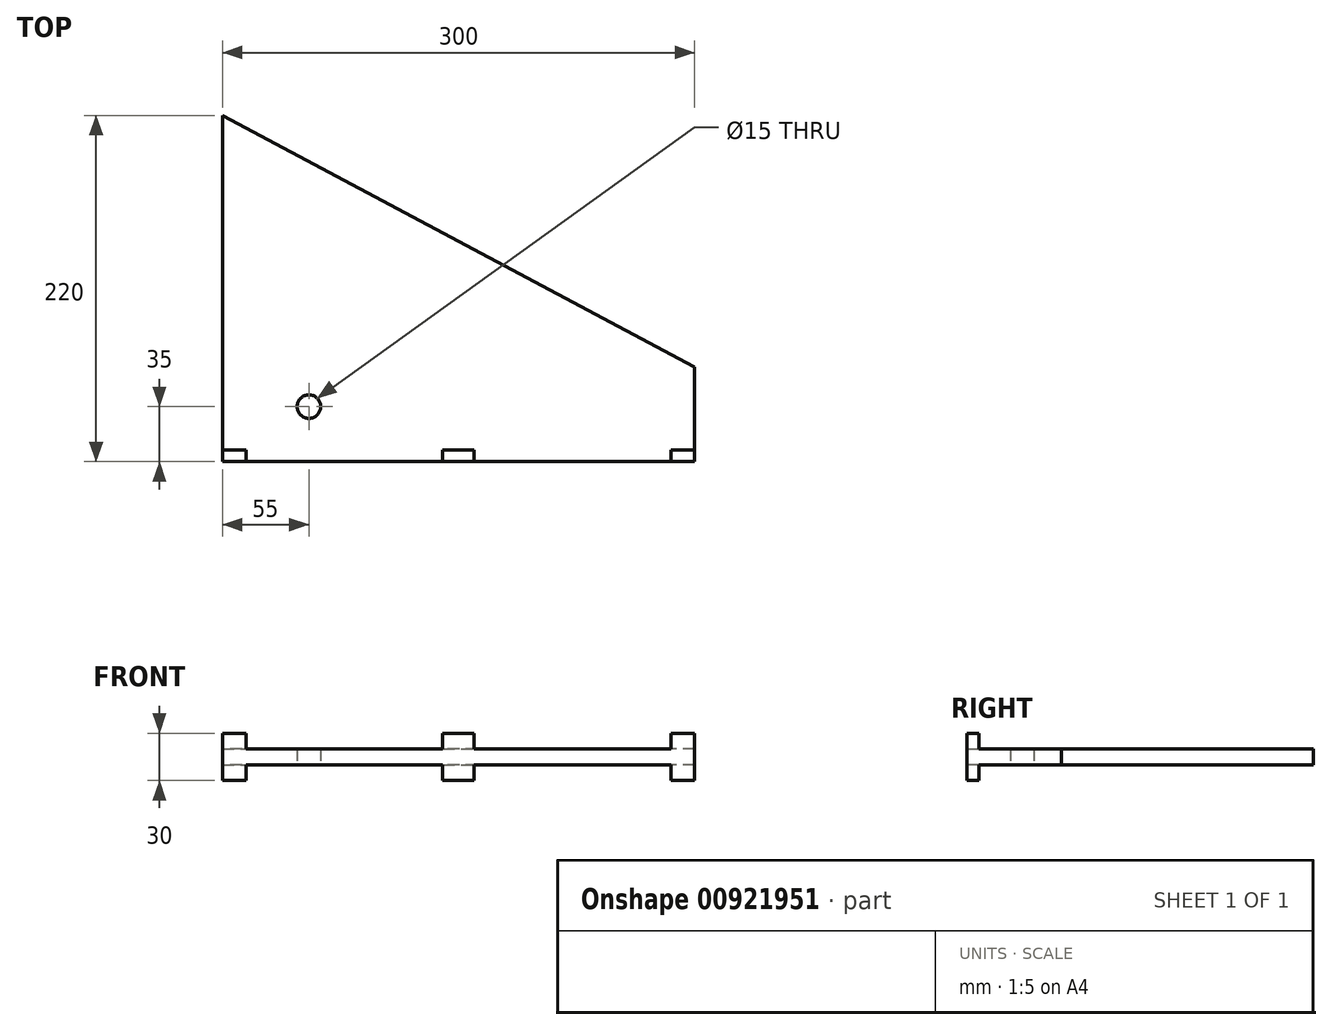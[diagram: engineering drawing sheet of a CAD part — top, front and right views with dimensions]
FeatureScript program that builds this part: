
annotation { "Feature Type Name" : "Feature", "Feature Type Description" : "" }
export const myFeature = defineFeature(function(context is Context, id is Id, definition is map)
    precondition{}
    {
        {
            var Q0;
            Q0=qCreatedBy(makeId("Top.planeOp"),FACE);
            var sketch = newSketch(context, id + "F0", { "sketchPlane" : qUnion([Q0])});
            skLineSegment(sketch, "E0", {"start": v(-150, 110) * mm, "end": v(-150, -110) * mm});
            skLineSegment(sketch, "E1", {"start": v(-150, -110) * mm, "end": v(150, -110) * mm});
            skLineSegment(sketch, "E2", {"start": v(150, -110) * mm, "end": v(150, -50) * mm});
            skLineSegment(sketch, "E3", {"start": v(150, -50) * mm, "end": v(-150, 110) * mm});
            skCircle(sketch, "E4", {"center": v(-95, -75) * mm, "radius": 7.5 * mm});
            skSolve(sketch);
        }
        {
            var Q0;
            Q0=makeQuery(id+"F0.imprint","IMPRINT",FACE,{"disambiguationData":[TD([[makeQuery(id+"F0.imprint","IMPRINT",EDGE,{"derivedFrom":sQuery(id+"F0.wireOp",EDGE,"E0")}),1.0]])]});
            extrude(context, id + "F1", {"entities" : qUnion([Q0]), "depth" : 10 * mm, "offsetDistance" : 25 * mm});
        }
        {
            var Q0;
            Q0=makeQuery(id+"F1.opExtrude","CAP_FACE",FACE,{"disambiguationData":[OSD([sQuery(id+"F0.wireOp",EDGE,"E0"),sQuery(id+"F0.wireOp",EDGE,"E1"),sQuery(id+"F0.wireOp",EDGE,"E2"),sQuery(id+"F0.wireOp",EDGE,"E3"),sQuery(id+"F0.wireOp",EDGE,"E4")])],"isStart":false});
            var sketch = newSketch(context, id + "F2", { "sketchPlane" : qUnion([Q0])});
            skLineSegment(sketch, "E5", {"start": v(-150, -110) * mm, "end": v(-150, -102.5) * mm});
            skLineSegment(sketch, "E6", {"start": v(-150, -102.5) * mm, "end": v(-135, -102.5) * mm});
            skLineSegment(sketch, "E7", {"start": v(-135, -102.5) * mm, "end": v(-135, -110) * mm});
            skLineSegment(sketch, "E8", {"start": v(-135, -110) * mm, "end": v(-150, -110) * mm});
            skLineSegment(sketch, "E9", {"start": v(150, -110) * mm, "end": v(150, -102.5) * mm});
            skLineSegment(sketch, "E10", {"start": v(150, -102.5) * mm, "end": v(135, -102.5) * mm});
            skLineSegment(sketch, "E11", {"start": v(135, -102.5) * mm, "end": v(135, -110) * mm});
            skLineSegment(sketch, "E12", {"start": v(135, -110) * mm, "end": v(150, -110) * mm});
            skLineSegment(sketch, "E13", {"start": v(-10, -110) * mm, "end": v(-10, -102.5) * mm});
            skLineSegment(sketch, "E14", {"start": v(-10, -102.5) * mm, "end": v(10, -102.5) * mm});
            skLineSegment(sketch, "E15", {"start": v(10, -102.5) * mm, "end": v(10, -110) * mm});
            skPoint(sketch, "E15.endSnap0", {"position": v(0, -110) * mm});
            skLineSegment(sketch, "E16", {"start": v(10, -110) * mm, "end": v(-10, -110) * mm});
            skSolve(sketch);
        }
        {
            var Q0;
            Q0 = qSketchRegion(id + "F2", true);
            extrude(context, id + "F3", {"entities" : qUnion([Q0]), "operationType" : NewBodyOperationType.ADD, "depth" : 10 * mm, "offsetDistance" : 25 * mm});
        }
        {
            var Q0;
            Q0=makeQuery(id+"F1.opExtrude","CAP_FACE",FACE,{"disambiguationData":[OSD([sQuery(id+"F0.wireOp",EDGE,"E0"),sQuery(id+"F0.wireOp",EDGE,"E1"),sQuery(id+"F0.wireOp",EDGE,"E2"),sQuery(id+"F0.wireOp",EDGE,"E3"),sQuery(id+"F0.wireOp",EDGE,"E4")])],"isStart":true});
            var sketch = newSketch(context, id + "F4", { "sketchPlane" : qUnion([Q0])});
            skLineSegment(sketch, "E17", {"start": v(-150, 110) * mm, "end": v(-150, 102.5) * mm});
            skLineSegment(sketch, "E18", {"start": v(-150, 102.5) * mm, "end": v(-135, 102.5) * mm});
            skLineSegment(sketch, "E19", {"start": v(-135, 102.5) * mm, "end": v(-135, 110) * mm});
            skLineSegment(sketch, "E20", {"start": v(-135, 110) * mm, "end": v(-150, 110) * mm});
            skLineSegment(sketch, "E21", {"start": v(150, 110) * mm, "end": v(150, 102.5) * mm});
            skLineSegment(sketch, "E22", {"start": v(150, 102.5) * mm, "end": v(135, 102.5) * mm});
            skLineSegment(sketch, "E23", {"start": v(135, 102.5) * mm, "end": v(135, 110) * mm});
            skLineSegment(sketch, "E24", {"start": v(135, 110) * mm, "end": v(150, 110) * mm});
            skLineSegment(sketch, "E25", {"start": v(-10, 110) * mm, "end": v(-10, 102.5) * mm});
            skLineSegment(sketch, "E26", {"start": v(-10, 102.5) * mm, "end": v(10, 102.5) * mm});
            skLineSegment(sketch, "E27", {"start": v(10, 102.5) * mm, "end": v(10, 110) * mm});
            skLineSegment(sketch, "E28", {"start": v(10, 110) * mm, "end": v(-10, 110) * mm});
            skSolve(sketch);
        }
        {
            var Q0;
            Q0 = qSketchRegion(id + "F4", true);
            extrude(context, id + "F5", {"entities" : qUnion([Q0]), "operationType" : NewBodyOperationType.ADD, "depth" : 10 * mm, "offsetDistance" : 25 * mm});
        }
    });
